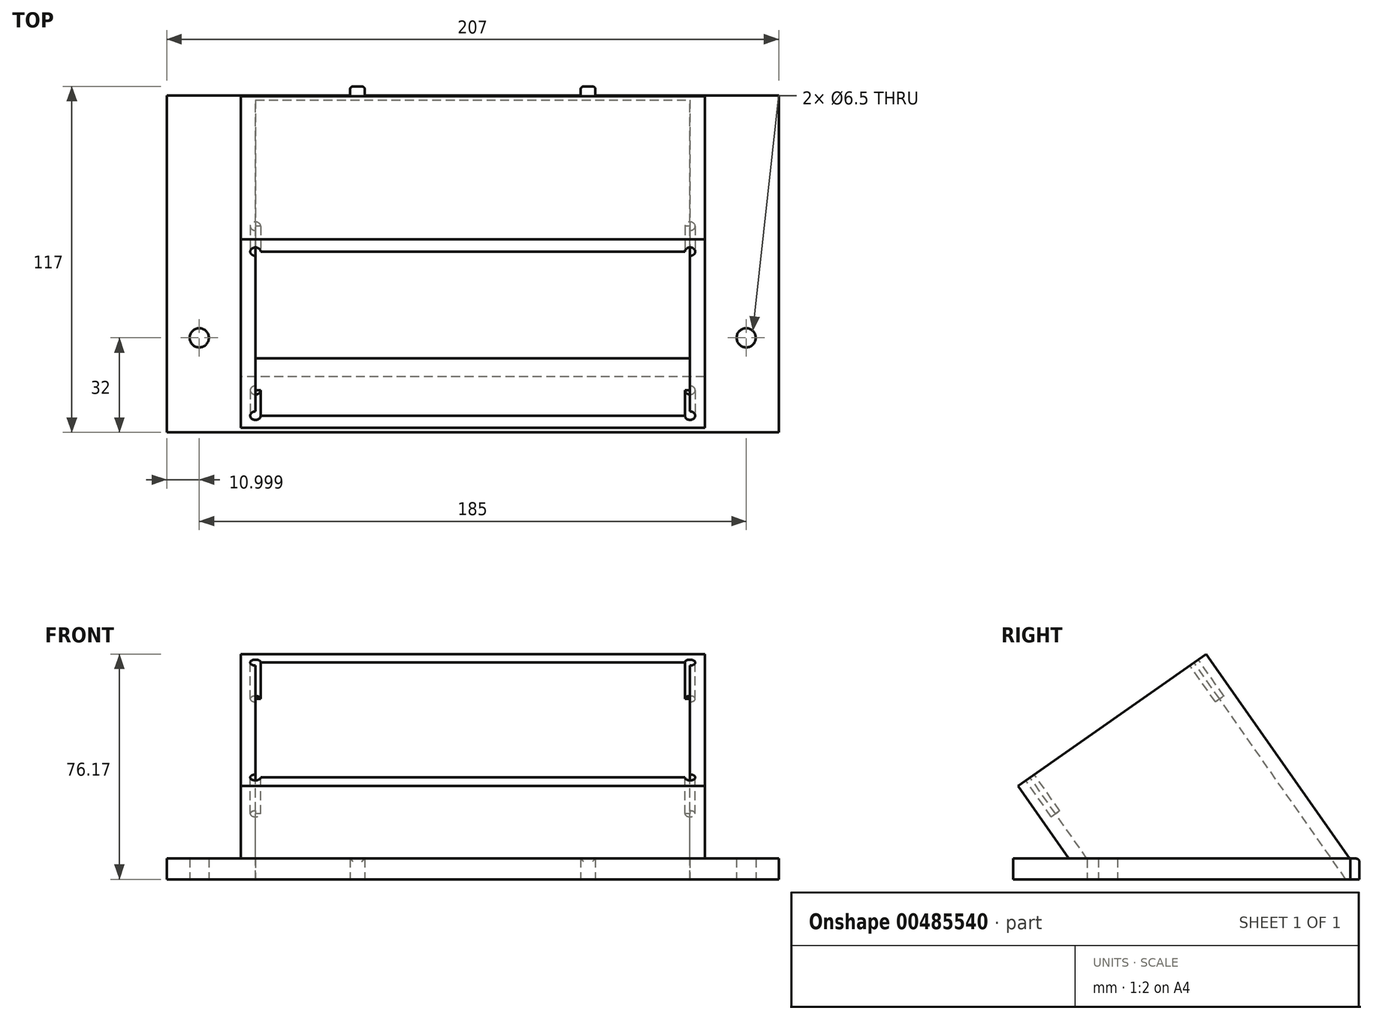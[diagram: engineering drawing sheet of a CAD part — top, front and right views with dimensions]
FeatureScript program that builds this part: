
annotation { "Feature Type Name" : "Feature", "Feature Type Description" : "" }
export const myFeature = defineFeature(function(context is Context, id is Id, definition is map)
    precondition{}
    {
        {
            var Q0;
            Q0=qCreatedBy(makeId("Top.planeOp"),FACE);
            var sketch = newSketch(context, id + "F0", { "sketchPlane" : qUnion([Q0])});
            skCircle(sketch, "E0", {"center": v(-20.26, 0) * mm, "radius": 3.25 * mm});
            skCircle(sketch, "E1", {"center": v(164.74, 0) * mm, "radius": 3.25 * mm});
            skLineSegment(sketch, "E2.bottom", {"start": v(-31.26, 82) * mm, "end": v(175.74, 82) * mm});
            skLineSegment(sketch, "E2.top", {"start": v(-31.26, -32) * mm, "end": v(175.74, -32) * mm});
            skLineSegment(sketch, "E2.left", {"start": v(-31.26, 82) * mm, "end": v(-31.26, -32) * mm});
            skLineSegment(sketch, "E2.right", {"start": v(175.74, 82) * mm, "end": v(175.74, -32) * mm});
            skLineSegment(sketch, "E3.bottom", {"start": v(-1.26, -7) * mm, "end": v(145.74, -7) * mm});
            skLineSegment(sketch, "E3.top", {"start": v(-1.26, 67) * mm, "end": v(145.74, 67) * mm});
            skLineSegment(sketch, "E3.left", {"start": v(-1.26, -7) * mm, "end": v(-1.26, 67) * mm});
            skLineSegment(sketch, "E3.right", {"start": v(145.74, -7) * mm, "end": v(145.74, 67) * mm});
            skLineSegment(sketch, "E4.bottom", {"start": v(30.74, 82) * mm, "end": v(35.74, 82) * mm});
            skLineSegment(sketch, "E4.top", {"start": v(30.74, 85) * mm, "end": v(35.74, 85) * mm});
            skLineSegment(sketch, "E4.left", {"start": v(30.74, 82) * mm, "end": v(30.74, 85) * mm});
            skLineSegment(sketch, "E4.right", {"start": v(35.74, 82) * mm, "end": v(35.74, 85) * mm});
            skLineSegment(sketch, "E5.bottom", {"start": v(108.74, 82) * mm, "end": v(113.74, 82) * mm});
            skLineSegment(sketch, "E5.top", {"start": v(108.74, 85) * mm, "end": v(113.74, 85) * mm});
            skLineSegment(sketch, "E5.left", {"start": v(108.74, 82) * mm, "end": v(108.74, 85) * mm});
            skLineSegment(sketch, "E5.right", {"start": v(113.74, 82) * mm, "end": v(113.74, 85) * mm});
            skSolve(sketch);
        }
        {
            var Q0;
            Q0 = qSketchRegion(id + "F0", true);
            extrude(context, id + "F1", {"entities" : qUnion([Q0]), "depth" : 7 * mm});
        }
        {
            var Q0;
            Q0=makeQuery(id+"F1.opExtrude","CAP_FACE",FACE,{"disambiguationData":[OSD([sQuery(id+"F0.wireOp",EDGE,"E0"),sQuery(id+"F0.wireOp",EDGE,"E1"),sQuery(id+"F0.wireOp",EDGE,"E2.bottom"),sQuery(id+"F0.wireOp",EDGE,"E2.top"),sQuery(id+"F0.wireOp",EDGE,"E2.left"),sQuery(id+"F0.wireOp",EDGE,"E2.right"),sQuery(id+"F0.wireOp",EDGE,"zIWrt8qD-0JgG-C9tS-MdOE-bdcsCjTpsGvl.top"),sQuery(id+"F0.wireOp",EDGE,"zIWrt8qD-0JgG-C9tS-MdOE-bdcsCjTpsGvl.left"),sQuery(id+"F0.wireOp",EDGE,"zIWrt8qD-0JgG-C9tS-MdOE-bdcsCjTpsGvl.right"),sQuery(id+"F0.wireOp",EDGE,"WT34eTZ0-hoBI-ZFRB-5qk9-YiIaJovB5DUL.top"),sQuery(id+"F0.wireOp",EDGE,"WT34eTZ0-hoBI-ZFRB-5qk9-YiIaJovB5DUL.left"),sQuery(id+"F0.wireOp",EDGE,"WT34eTZ0-hoBI-ZFRB-5qk9-YiIaJovB5DUL.right"),sQuery(id+"F0.wireOp",EDGE,"E3.bottom"),sQuery(id+"F0.wireOp",EDGE,"E3.top"),sQuery(id+"F0.wireOp",EDGE,"E3.left"),sQuery(id+"F0.wireOp",EDGE,"E3.right")])],"isStart":false});
            var sketch = newSketch(context, id + "F2", { "sketchPlane" : qUnion([Q0])});
            skPoint(sketch, "E6", {"position": v(72.24, 67) * mm});
            skLineSegment(sketch, "E7", {"start": v(72.24, 67) * mm, "end": v(-0.26, 82) * mm});
            skSolve(sketch);
        }
        {
            var Q0;
            Q0=qCreatedBy(makeId("Right.planeOp"),FACE);
            var sketch = newSketch(context, id + "F3", { "sketchPlane" : qUnion([Q0])});
            skLineSegment(sketch, "E8", {"start": v(81.68, 7) * mm, "end": v(33.25, 76.17) * mm});
            skLineSegment(sketch, "E9", {"start": v(-13.22, 7) * mm, "end": v(-30.43, 31.57) * mm});
            skLineSegment(sketch, "E10", {"start": v(-30.43, 31.57) * mm, "end": v(33.25, 76.17) * mm});
            skLineSegment(sketch, "E11", {"start": v(81.68, 7) * mm, "end": v(-13.22, 7) * mm});
            skSolve(sketch);
        }
        {
            var Q0;
            Q0 = qSketchRegion(id + "F3", true);
            extrude(context, id + "F4", {"entities" : qUnion([Q0]), "operationType" : NewBodyOperationType.ADD, "depth" : 150.74 * mm, "hasSecondDirection" : true, "secondDirectionOppositeDirection" : true, "secondDirectionDepth" : 6.26 * mm});
        }
        {
            var Q0;
            Q0=makeQuery(id+"F4.opExtrude","SWEPT_FACE",FACE,{"disambiguationData":[OSD([sQuery(id+"F3.wireOp",EDGE,"E10")])]});
            var sketch = newSketch(context, id + "F5", { "sketchPlane" : qUnion([Q0])});
            skLineSegment(sketch, "E12.bottom", {"start": v(-1.26, -1.82) * mm, "end": v(145.74, -1.82) * mm});
            skLineSegment(sketch, "E12.top", {"start": v(-1.26, 65.93) * mm, "end": v(145.74, 65.93) * mm});
            skLineSegment(sketch, "E12.left", {"start": v(-1.26, -1.82) * mm, "end": v(-1.26, 65.93) * mm});
            skLineSegment(sketch, "E12.right", {"start": v(145.74, -1.82) * mm, "end": v(145.74, 65.93) * mm});
            skSolve(sketch);
        }
        {
            var Q0;
            Q0=makeQuery(id+"F5.imprint","IMPRINT",FACE,{"disambiguationData":[TD([[makeQuery(id+"F5.imprint","IMPRINT",EDGE,{"derivedFrom":sQuery(id+"F5.wireOp",EDGE,"E12.bottom")}),1.0]])]});
            extrude(context, id + "F6", {"entities" : qUnion([Q0]), "operationType" : NewBodyOperationType.REMOVE, "oppositeDirection" : true, "depth" : 156.2 * mm});
        }
        {
            var Q0;
            Q0=makeQuery(id+"F1.opExtrude","CAP_EDGE",EDGE,{"disambiguationData":[OSD([sQuery(id+"F0.wireOp",EDGE,"E5.top")])],"isStart":false});
            var Q1;
            Q1=makeQuery(id+"F1.opExtrude","CAP_EDGE",EDGE,{"disambiguationData":[OSD([sQuery(id+"F0.wireOp",EDGE,"E4.top")])],"isStart":false});
            var Q2;
            Q2=makeQuery(id+"F1.opExtrude","SWEPT_EDGE",EDGE,{"disambiguationData":[OSD([sQuery(id+"F0.wireOp",EDGE,"E4.top"),sQuery(id+"F0.wireOp",EDGE,"E4.right")])]});
            var Q3;
            Q3=makeQuery(id+"F1.opExtrude","SWEPT_EDGE",EDGE,{"disambiguationData":[OSD([sQuery(id+"F0.wireOp",EDGE,"E4.top"),sQuery(id+"F0.wireOp",EDGE,"E4.left")])]});
            var Q4;
            Q4=makeQuery(id+"F1.opExtrude","SWEPT_EDGE",EDGE,{"disambiguationData":[OSD([sQuery(id+"F0.wireOp",EDGE,"E5.top"),sQuery(id+"F0.wireOp",EDGE,"E5.left")])]});
            var Q5;
            Q5=makeQuery(id+"F1.opExtrude","SWEPT_EDGE",EDGE,{"disambiguationData":[OSD([sQuery(id+"F0.wireOp",EDGE,"E5.top"),sQuery(id+"F0.wireOp",EDGE,"E5.right")])]});
            fillet(context, id + "F7", {"entities" : qUnion([Q0, Q1, Q2, Q3, Q4, Q5]), "radius" : 1 * mm, "tangentPropagation" : true, "allowEdgeOverflow" : false});
        }
        {
            var Q0;
            Q0=makeQuery(id+"F4.opExtrude","SWEPT_FACE",FACE,{"disambiguationData":[OSD([sQuery(id+"F3.wireOp",EDGE,"E10")])]});
            var sketch = newSketch(context, id + "F8", { "sketchPlane" : qUnion([Q0])});
            skArc(sketch, "E13", {"start": v(150.74, -1.82) * mm, "mid": v(142.2, 1.72) * mm, "end": v(145.74, -6.82) * mm});
            skArc(sketch, "E14", {"start": v(145.74, 70.93) * mm, "mid": v(142.2, 62.4) * mm, "end": v(150.74, 65.93) * mm});
            skArc(sketch, "E15", {"start": v(-6.26, 65.93) * mm, "mid": v(2.27, 62.4) * mm, "end": v(-1.26, 70.93) * mm});
            skArc(sketch, "E16", {"start": v(-1.26, -6.82) * mm, "mid": v(2.27, 1.72) * mm, "end": v(-6.26, -1.82) * mm});
            skSolve(sketch);
        }
        {
            var Q0;
            Q0 = qSketchRegion(id + "F8", true);
            var Q1;
            {var subQ0=sQuery(id+"F8.wireOp",EDGE,"Z9M8HE5b-TqbY-U2Sx-4Tjp-rA6B6peJnGQj");var subQ1=makeQuery(id+"F6.boolean.opBoolean","COPY",EDGE,{"derivedFrom":makeQuery(id+"F6.opExtrude","CAP_EDGE",EDGE,{"disambiguationData":[OSD([sQuery(id+"F5.wireOp",EDGE,"E12.bottom")])],"isStart":true})});var subQ2=makeQuery(id+"F8.imprint","INTERSECT",VERTEX,{"derivedFrom":[subQ1,subQ0]});Q1=makeQuery(id+"F8.imprint","IMPRINT",FACE,{"disambiguationData":[TD([[makeQuery(id+"F8.imprint","IMPRINT",EDGE,{"disambiguationData":[TD([[subQ2,-1.0]])],"derivedFrom":subQ0}),1.0]])]});}
            var Q2;
            {var subQ0=sQuery(id+"F3.wireOp",EDGE,"E10");var subQ1=makeQuery(id+"F4.opExtrude","CAP_EDGE",EDGE,{"disambiguationData":[OSD([subQ0])],"isStart":true});var subQ4=sQuery(id+"F8.wireOp",EDGE,"Z9M8HE5b-TqbY-U2Sx-4Tjp-rA6B6peJnGQj");var subQ9=makeQuery(id+"F8.imprint","INTERSECT",VERTEX,{"disambiguationData":[OD(1.0)],"derivedFrom":[subQ1,subQ4]});Q2=makeQuery(id+"F8.imprint","IMPRINT",FACE,{"disambiguationData":[TD([[makeQuery(id+"F8.imprint","IMPRINT",EDGE,{"disambiguationData":[TD([[subQ9,1.0]])],"derivedFrom":subQ4}),1.0]])]});}
            var Q3;
            {var subQ0=sQuery(id+"F3.wireOp",EDGE,"E10");var subQ1=makeQuery(id+"F4.opExtrude","CAP_EDGE",EDGE,{"disambiguationData":[OSD([subQ0])],"isStart":true});var subQ4=sQuery(id+"F8.wireOp",EDGE,"E15");var subQ5=makeQuery(id+"F8.imprint","INTERSECT",VERTEX,{"derivedFrom":[subQ1,subQ4]});Q3=makeQuery(id+"F8.imprint","IMPRINT",FACE,{"disambiguationData":[TD([[makeQuery(id+"F8.imprint","IMPRINT",EDGE,{"disambiguationData":[TD([[subQ5,-1.0]])],"derivedFrom":subQ4}),1.0]])]});}
            var Q4;
            {var subQ0=sQuery(id+"F8.wireOp",EDGE,"E15");var subQ1=makeQuery(id+"F6.boolean.opBoolean","COPY",EDGE,{"derivedFrom":makeQuery(id+"F6.opExtrude","CAP_EDGE",EDGE,{"disambiguationData":[OSD([sQuery(id+"F5.wireOp",EDGE,"E12.left")])],"isStart":true})});var subQ2=makeQuery(id+"F8.imprint","INTERSECT",VERTEX,{"derivedFrom":[subQ1,subQ0]});Q4=makeQuery(id+"F8.imprint","IMPRINT",FACE,{"disambiguationData":[TD([[makeQuery(id+"F8.imprint","IMPRINT",EDGE,{"disambiguationData":[TD([[subQ2,-1.0]])],"derivedFrom":subQ0}),1.0]])]});}
            var Q5;
            {var subQ0=sQuery(id+"F8.wireOp",EDGE,"E13");var subQ1=makeQuery(id+"F6.boolean.opBoolean","COPY",EDGE,{"derivedFrom":makeQuery(id+"F6.opExtrude","CAP_EDGE",EDGE,{"disambiguationData":[OSD([sQuery(id+"F5.wireOp",EDGE,"E12.right")])],"isStart":true})});var subQ2=makeQuery(id+"F8.imprint","INTERSECT",VERTEX,{"derivedFrom":[subQ1,subQ0]});Q5=makeQuery(id+"F8.imprint","IMPRINT",FACE,{"disambiguationData":[TD([[makeQuery(id+"F8.imprint","IMPRINT",EDGE,{"disambiguationData":[TD([[subQ2,-1.0]])],"derivedFrom":subQ0}),1.0]])]});}
            var Q6;
            {var subQ0=sQuery(id+"F8.wireOp",EDGE,"E14");var subQ1=makeQuery(id+"F6.boolean.opBoolean","COPY",EDGE,{"derivedFrom":makeQuery(id+"F6.opExtrude","CAP_EDGE",EDGE,{"disambiguationData":[OSD([sQuery(id+"F5.wireOp",EDGE,"E12.top")])],"isStart":true})});var subQ2=makeQuery(id+"F8.imprint","INTERSECT",VERTEX,{"derivedFrom":[subQ1,subQ0]});Q6=makeQuery(id+"F8.imprint","IMPRINT",FACE,{"disambiguationData":[TD([[makeQuery(id+"F8.imprint","IMPRINT",EDGE,{"disambiguationData":[TD([[subQ2,-1.0]])],"derivedFrom":subQ0}),1.0]])]});}
            var Q7;
            {var subQ0=sQuery(id+"F3.wireOp",EDGE,"E10");var subQ1=makeQuery(id+"F4.opExtrude","CAP_EDGE",EDGE,{"disambiguationData":[OSD([subQ0])],"isStart":false});var subQ4=sQuery(id+"F8.wireOp",EDGE,"E13");var subQ5=makeQuery(id+"F8.imprint","INTERSECT",VERTEX,{"derivedFrom":[subQ1,subQ4]});Q7=makeQuery(id+"F8.imprint","IMPRINT",FACE,{"disambiguationData":[TD([[makeQuery(id+"F8.imprint","IMPRINT",EDGE,{"disambiguationData":[TD([[subQ5,-1.0]])],"derivedFrom":subQ4}),1.0]])]});}
            var Q8;
            {var subQ0=sQuery(id+"F3.wireOp",EDGE,"E10");var subQ1=makeQuery(id+"F4.opExtrude","CAP_EDGE",EDGE,{"disambiguationData":[OSD([subQ0])],"isStart":false});var subQ4=sQuery(id+"F8.wireOp",EDGE,"E14");var subQ11=makeQuery(id+"F8.imprint","INTERSECT",VERTEX,{"derivedFrom":[subQ1,subQ4]});Q8=makeQuery(id+"F8.imprint","IMPRINT",FACE,{"disambiguationData":[TD([[makeQuery(id+"F8.imprint","IMPRINT",EDGE,{"disambiguationData":[TD([[subQ11,1.0]])],"derivedFrom":subQ4}),1.0]])]});}
            var Q9;
            {var subQ0=sQuery(id+"F8.wireOp",EDGE,"E16");var subQ1=makeQuery(id+"F6.boolean.opBoolean","COPY",EDGE,{"derivedFrom":makeQuery(id+"F6.opExtrude","CAP_EDGE",EDGE,{"disambiguationData":[OSD([sQuery(id+"F5.wireOp",EDGE,"E12.bottom")])],"isStart":true})});var subQ2=makeQuery(id+"F8.imprint","INTERSECT",VERTEX,{"derivedFrom":[subQ1,subQ0]});Q9=makeQuery(id+"F8.imprint","IMPRINT",FACE,{"disambiguationData":[TD([[makeQuery(id+"F8.imprint","IMPRINT",EDGE,{"disambiguationData":[TD([[subQ2,-1.0]])],"derivedFrom":subQ0}),1.0]])]});}
            extrude(context, id + "F9", {"entities" : qUnion([Q0, Q1, Q2, Q3, Q4, Q5, Q6, Q7, Q8, Q9]), "operationType" : NewBodyOperationType.ADD, "oppositeDirection" : true, "depth" : 15 * mm});
        }
        {
            var Q0;
            {var subQ0=sQuery(id+"F3.wireOp",EDGE,"E10");var subQ1=sQuery(id+"F3.wireOp",EDGE,"E9");var subQ2=sQuery(id+"F3.wireOp",EDGE,"E8");Q0=makeQuery(id+"F9.boolean.opBoolean","MERGE",FACE,{"derivedFrom":[makeQuery(id+"F4.opExtrude","SWEPT_FACE",FACE,{"disambiguationData":[OSD([subQ0])]}),makeQuery(id+"F9.opExtrude","CAP_FACE",FACE,{"disambiguationData":[OSD([subQ1,subQ0,sQuery(id+"F8.wireOp",EDGE,"E13")])],"isStart":true}),makeQuery(id+"F9.opExtrude","CAP_FACE",FACE,{"disambiguationData":[OSD([subQ2,subQ0,sQuery(id+"F8.wireOp",EDGE,"E14")])],"isStart":true}),makeQuery(id+"F9.opExtrude","CAP_FACE",FACE,{"disambiguationData":[OSD([subQ2,subQ0,sQuery(id+"F8.wireOp",EDGE,"E15")])],"isStart":true}),makeQuery(id+"F9.opExtrude","CAP_FACE",FACE,{"disambiguationData":[OSD([subQ1,subQ0,sQuery(id+"F8.wireOp",EDGE,"Z9M8HE5b-TqbY-U2Sx-4Tjp-rA6B6peJnGQj")])],"isStart":true})]});}
            var sketch = newSketch(context, id + "F10", { "sketchPlane" : qUnion([Q0])});
            skCircle(sketch, "E17", {"center": v(145.74, -1.82) * mm, "radius": 1.75 * mm});
            skCircle(sketch, "E18", {"center": v(-1.26, 65.93) * mm, "radius": 1.75 * mm});
            skCircle(sketch, "E19", {"center": v(145.74, 65.93) * mm, "radius": 1.75 * mm});
            skCircle(sketch, "E20", {"center": v(-1.26, -1.82) * mm, "radius": 1.75 * mm});
            skSolve(sketch);
        }
        {
            var Q0;
            Q0=makeQuery(id+"F10.imprint","IMPRINT",FACE,{"disambiguationData":[TD([[makeQuery(id+"F10.imprint","IMPRINT",EDGE,{"derivedFrom":sQuery(id+"F10.wireOp",EDGE,"E17")}),1.0]])]});
            var Q1;
            Q1=makeQuery(id+"F10.imprint","IMPRINT",FACE,{"disambiguationData":[TD([[makeQuery(id+"F10.imprint","IMPRINT",EDGE,{"derivedFrom":sQuery(id+"F10.wireOp",EDGE,"E19")}),1.0]])]});
            var Q2;
            Q2=makeQuery(id+"F10.imprint","IMPRINT",FACE,{"disambiguationData":[TD([[makeQuery(id+"F10.imprint","IMPRINT",EDGE,{"derivedFrom":sQuery(id+"F10.wireOp",EDGE,"E18")}),1.0]])]});
            var Q3;
            Q3=makeQuery(id+"F10.imprint","IMPRINT",FACE,{"disambiguationData":[TD([[makeQuery(id+"F10.imprint","IMPRINT",EDGE,{"derivedFrom":sQuery(id+"F10.wireOp",EDGE,"E20")}),1.0]])]});
            extrude(context, id + "F11", {"entities" : qUnion([Q0, Q1, Q2, Q3]), "operationType" : NewBodyOperationType.REMOVE, "oppositeDirection" : true, "depth" : 15 * mm});
        }
    });
